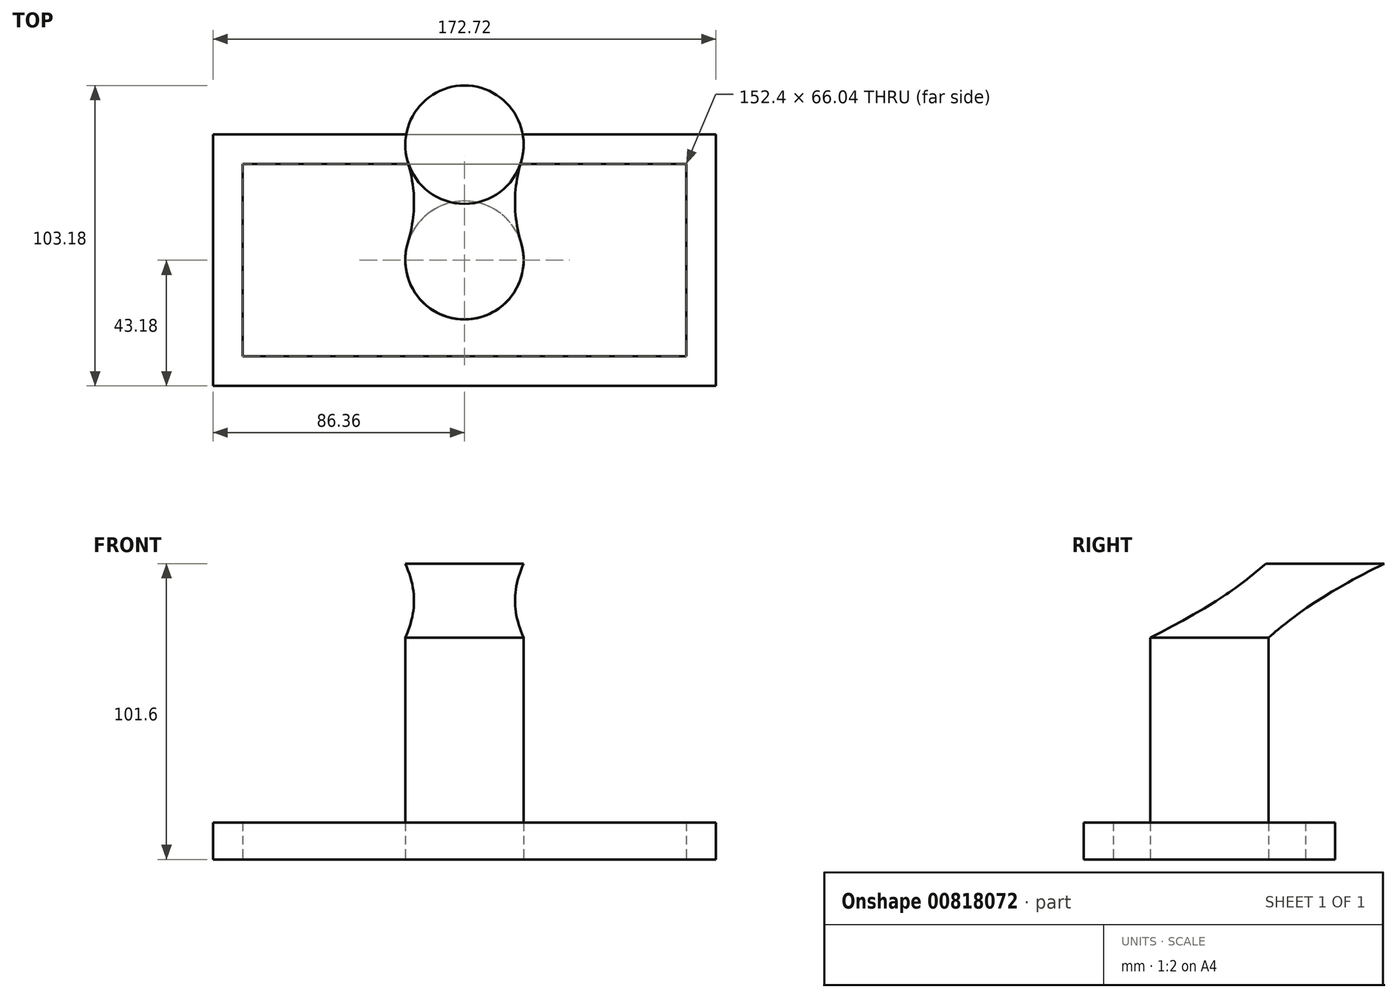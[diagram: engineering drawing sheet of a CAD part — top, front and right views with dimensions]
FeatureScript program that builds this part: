
annotation { "Feature Type Name" : "Feature", "Feature Type Description" : "" }
export const myFeature = defineFeature(function(context is Context, id is Id, definition is map)
    precondition{}
    {
        {
            var Q0;
            Q0=qCreatedBy(makeId("Top.planeOp"),FACE);
            var sketch = newSketch(context, id + "F0", { "sketchPlane" : qUnion([Q0])});
            skLineSegment(sketch, "E0.bottom", {"start": v(-86.36, 48.26) * mm, "end": v(86.36, 48.26) * mm});
            skLineSegment(sketch, "E0.top", {"start": v(-86.36, -38.1) * mm, "end": v(86.36, -38.1) * mm});
            skLineSegment(sketch, "E0.left", {"start": v(-86.36, 48.26) * mm, "end": v(-86.36, -38.1) * mm});
            skLineSegment(sketch, "E0.right", {"start": v(86.36, 48.26) * mm, "end": v(86.36, -38.1) * mm});
            skLineSegment(sketch, "E1.bottom", {"start": v(-76.2, 38.1) * mm, "end": v(76.2, 38.1) * mm});
            skLineSegment(sketch, "E1.top", {"start": v(-76.2, -27.94) * mm, "end": v(76.2, -27.94) * mm});
            skLineSegment(sketch, "E1.left", {"start": v(-76.2, 38.1) * mm, "end": v(-76.2, -27.94) * mm});
            skLineSegment(sketch, "E1.right", {"start": v(76.2, 38.1) * mm, "end": v(76.2, -27.94) * mm});
            skSolve(sketch);
        }
        {
            var Q0;
            Q0=makeQuery(id+"F0.imprint","IMPRINT",FACE,{"disambiguationData":[TD([[makeQuery(id+"F0.imprint","IMPRINT",EDGE,{"derivedFrom":sQuery(id+"F0.wireOp",EDGE,"E0.bottom")}),-1.0]])]});
            extrude(context, id + "F1", {"entities" : qUnion([Q0]), "depth" : 12.7 * mm, "offsetDistance" : 25.4 * mm});
        }
        {
            var Q0;
            Q0=qCreatedBy(makeId("Top.planeOp"),FACE);
            var sketch = newSketch(context, id + "F2", { "sketchPlane" : qUnion([Q0])});
            skCircle(sketch, "E2", {"center": v(0, 5.08) * mm, "radius": 20.32 * mm});
            skSolve(sketch);
        }
        {
            var Q0;
            Q0=makeQuery(id+"F2.imprint","IMPRINT",FACE,{"disambiguationData":[TD([[makeQuery(id+"F2.imprint","IMPRINT",EDGE,{"derivedFrom":sQuery(id+"F2.wireOp",EDGE,"E2")}),1.0]])]});
            extrude(context, id + "F3", {"entities" : qUnion([Q0]), "depth" : 76.2 * mm, "offsetDistance" : 25.4 * mm});
        }
        {
            var Q0;
            Q0=qCreatedBy(makeId("Top.planeOp"),FACE);
            cPlane(context, id + "F4", {"entities" : qUnion([Q0]), "cplaneType" : CPlaneType.OFFSET, "offset" : 101.6 * mm, "width" : 152.4 * mm, "height" : 152.4 * mm});
        }
        {
            var Q0;
            Q0=qCreatedBy(id+"F4.planeOp",FACE);
            var sketch = newSketch(context, id + "F5", { "sketchPlane" : qUnion([Q0])});
            skCircle(sketch, "E3", {"center": v(0, 44.76) * mm, "radius": 20.32 * mm});
            skSolve(sketch);
        }
        {
            var Q0;
            Q0=makeQuery(id+"F5.imprint","IMPRINT",FACE,{"disambiguationData":[TD([[makeQuery(id+"F5.imprint","IMPRINT",EDGE,{"derivedFrom":sQuery(id+"F5.wireOp",EDGE,"E3")}),1.0]])]});
            var Q1;
            Q1=makeQuery(id+"F3.opExtrude","CAP_FACE",FACE,{"disambiguationData":[OSD([sQuery(id+"F2.wireOp",EDGE,"E2")])],"isStart":false});
            loft(context, id + "F6", {"sheetProfilesArray" : [{ "sheetProfileEntities" : qUnion([Q0]) }, { "sheetProfileEntities" : qUnion([Q1]) }]});
        }
    });
